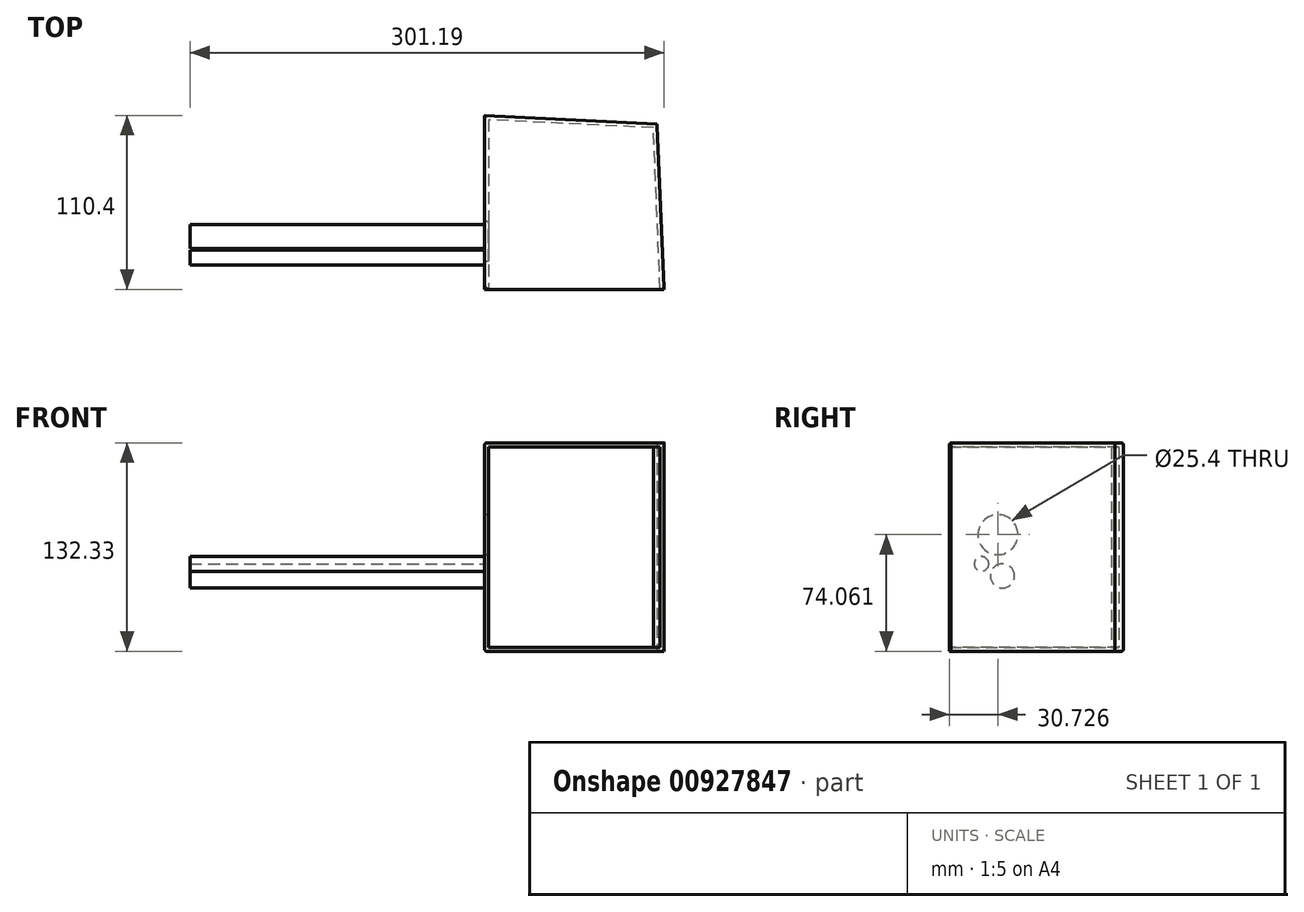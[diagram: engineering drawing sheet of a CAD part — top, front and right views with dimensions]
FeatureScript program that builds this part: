
annotation { "Feature Type Name" : "Feature", "Feature Type Description" : "" }
export const myFeature = defineFeature(function(context is Context, id is Id, definition is map)
    precondition{}
    {
        {
            var Q0;
            Q0=qCreatedBy(makeId("Top.planeOp"),FACE);
            var sketch = newSketch(context, id + "F0", { "sketchPlane" : qUnion([Q0])});
            skLineSegment(sketch, "E0", {"start": v(-57.18, 63.24) * mm, "end": v(-57.18, -47.16) * mm});
            skLineSegment(sketch, "E1", {"start": v(-57.18, -47.16) * mm, "end": v(56.8, -47.16) * mm});
            skLineSegment(sketch, "E2", {"start": v(56.8, -47.16) * mm, "end": v(52.32, 57.96) * mm});
            skLineSegment(sketch, "E3", {"start": v(52.32, 57.96) * mm, "end": v(-57.18, 63.24) * mm});
            skSolve(sketch);
        }
        {
            var Q0;
            Q0=makeQuery(id+"F0.imprint","IMPRINT",FACE,{"disambiguationData":[TD([[makeQuery(id+"F0.imprint","IMPRINT",EDGE,{"derivedFrom":sQuery(id+"F0.wireOp",EDGE,"E0")}),1.0]])]});
            extrude(context, id + "F1", {"entities" : qUnion([Q0]), "depth" : 132.33 * mm, "offsetDistance" : 25.4 * mm});
        }
        {
            var Q0;
            Q0=makeQuery(id+"F1.opExtrude","SWEPT_FACE",FACE,{"disambiguationData":[OSD([sQuery(id+"F0.wireOp",EDGE,"E1")])]});
            shell(context, id + "F2", {"entities" : qUnion([Q0]), "thickness" : 2.54 * mm});
        }
        {
            var Q0;
            Q0=makeQuery(id+"F1.opExtrude","SWEPT_FACE",FACE,{"disambiguationData":[OSD([sQuery(id+"F0.wireOp",EDGE,"E1")])]});
            extrude(context, id + "F3", {"entities" : qUnion([Q0]), "operationType" : NewBodyOperationType.ADD, "oppositeDirection" : true, "depth" : 0.76 * mm, "offsetDistance" : 25.4 * mm});
        }
        {
            var Q0;
            Q0=makeQuery(id+"F2.opShell","OFFSET_FACE",FACE,{"disambiguationData":[OSD([sQuery(id+"F0.wireOp",EDGE,"E0")])]});
            var sketch = newSketch(context, id + "F4", { "sketchPlane" : qUnion([Q0])});
            skCircle(sketch, "E4", {"center": v(-16.43, 74.06) * mm, "radius": 9.39 * mm});
            skSolve(sketch);
        }
        {
            var Q0;
            Q0=sQuery(id+"F4.wireOp",VERTEX,"E4.center");
            var Q1;
            Q1=makeQuery(id+"F1.opExtrude","SWEPT_BODY",BODY,{"disambiguationData":[OSD([sQuery(id+"F0.wireOp",EDGE,"E0"),sQuery(id+"F0.wireOp",EDGE,"E1"),sQuery(id+"F0.wireOp",EDGE,"E2"),sQuery(id+"F0.wireOp",EDGE,"E3")])]});
            hole(context, id + "F5", {"style" : HoleStyle.SIMPLE, "endStyle" : HoleEndStyle.BLIND, "holeDiameter" : 25.4 * mm, "majorDiameter" : 6.35 * mm, "holeDepth" : 5.08 * mm, "isTappedThrough" : true, "tappedDepth" : 12.7 * mm, "tapClearance" : 3, "locations" : qUnion([Q0]), "scope" : qUnion([Q1])});
        }
        {
            var Q0;
            Q0=makeQuery(id+"F1.opExtrude","SWEPT_FACE",FACE,{"disambiguationData":[OSD([sQuery(id+"F0.wireOp",EDGE,"E0")])]});
            var sketch = newSketch(context, id + "F6", { "sketchPlane" : qUnion([Q0])});
            skSolve(sketch);
        }
        {
            var Q0;
            Q0=makeQuery(id+"F2.opShell","OFFSET_FACE",FACE,{"disambiguationData":[OSD([sQuery(id+"F0.wireOp",EDGE,"E0")])]});
            var sketch = newSketch(context, id + "F7", { "sketchPlane" : qUnion([Q0])});
            skCircle(sketch, "E5", {"center": v(-13.54, 47.88) * mm, "radius": 7.72 * mm});
            skCircle(sketch, "E6", {"center": v(-26.86, 55.5) * mm, "radius": 4.64 * mm});
            skSolve(sketch);
        }
        {
            var Q0;
            {var subQ0=sQuery(id+"F0.wireOp",EDGE,"E0");Q0=makeQuery(id+"F6.imprint","IMPRINT",FACE,{"disambiguationData":[TD([[makeQuery(id+"F6.imprint","IMPRINT",EDGE,{"derivedFrom":makeQuery(id+"F1.opExtrude","CAP_EDGE",EDGE,{"disambiguationData":[OSD([subQ0])],"isStart":true})}),1.0]])]});}
            var sketch = newSketch(context, id + "F8", { "sketchPlane" : qUnion([Q0])});
            skSolve(sketch);
        }
        {
            var Q0;
            Q0=makeQuery(id+"F1.opExtrude","CAP_EDGE",EDGE,{"disambiguationData":[OSD([sQuery(id+"F0.wireOp",EDGE,"E0")])],"isStart":false});
            var Q1;
            Q1=makeQuery(id+"F1.opExtrude","CAP_EDGE",EDGE,{"disambiguationData":[OSD([sQuery(id+"F0.wireOp",EDGE,"E3")])],"isStart":false});
            var Q2;
            Q2=makeQuery(id+"F1.opExtrude","CAP_EDGE",EDGE,{"disambiguationData":[OSD([sQuery(id+"F0.wireOp",EDGE,"E1")])],"isStart":false});
            var Q3;
            Q3=makeQuery(id+"F1.opExtrude","CAP_EDGE",EDGE,{"disambiguationData":[OSD([sQuery(id+"F0.wireOp",EDGE,"E0")])],"isStart":true});
            var Q4;
            Q4=makeQuery(id+"F1.opExtrude","CAP_EDGE",EDGE,{"disambiguationData":[OSD([sQuery(id+"F0.wireOp",EDGE,"E2")])],"isStart":true});
            var Q5;
            Q5=makeQuery(id+"F1.opExtrude","CAP_EDGE",EDGE,{"disambiguationData":[OSD([sQuery(id+"F0.wireOp",EDGE,"E3")])],"isStart":true});
            fillet(context, id + "F9", {"entities" : qUnion([Q0, Q1, Q2, Q3, Q4, Q5]), "radius" : 1.23 * mm, "tangentPropagation" : true, "allowEdgeOverflow" : false});
        }
        {
            var Q0;
            Q0 = qSketchRegion(id + "F7", true);
            extrude(context, id + "F10", {"entities" : qUnion([Q0]), "operationType" : NewBodyOperationType.ADD, "oppositeDirection" : true, "depth" : 189.74 * mm, "offsetDistance" : 25.4 * mm});
        }
    });
